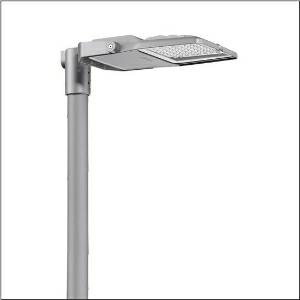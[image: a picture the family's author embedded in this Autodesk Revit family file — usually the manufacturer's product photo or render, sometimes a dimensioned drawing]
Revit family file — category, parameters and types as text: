
# Revit family: floodlight_fl_21_iq_mini___pl33t_5xa7771c2f3a_7d89
name_source: partatom
category: Lighting Fixtures
units: mm (PartAtom-declared; Revit-internal decimal feet)

## family parameters
Cut with Voids When Loaded = No
Host = Face
Light Source = No
Part Type = Normal
Room Calculation Point = No
Round Connector Dimension = Use Diameter
Shared = No

## types (1)
- --- (1 x LED, 12060 lm, 87.2 W, 3000K)
    Apparent Load = 87 VA
    CIE Flux Codes = 26 75 99 100 100
    Color Rendering = 70
    Color Temperature = 3000K
    Default Elevation = 1800 mm
    Description = Floodlight FL 21 iQ mini, floodlight, primary light control with lens, of PMMA, primary optical cover: protective disc, of toughened safety glass, transparent, light distribution: PL33T, light emission: direct distribution, installation type: surface-mounted, lamps: LED, High Power LED, rated values: 12.060lm | 87,2W | 138,3lm/W (begin service life); end service life: 12.060lm | 92,1W; at 50% lumin. flux: 6.030lm | 40,1W | 150,4lm/W, colour temperature: 3000K, colour rendering: CRI > 70, light colour: 730, light setting 1 begin service life: 100% | 12.060lm | 87,2W | 138,3lm/W | 3.000K, light setting 1 end service life: 92,1W, further light settings possible, control: Auto-Match, Temp-Guard, Lumen-Switch, Night-Set, Smart-Wire, Light-Fading, Desk-Remote (wireless, voltage-free reading and setting of iQ features in the workshop via application-optimized NFC function/RFID function), optimised constant luminous flux control (CLO 2.0), pre-setting: linear dimming characteristic, with terminal, 6-pole, mains connection: 220..240V, AC, 50/60Hz, luminaire housing, of diecast aluminium, powder-coated, SITECO metallic grey (DB 702S), corrosivity category C5 mid according to DIN EN ISO 12944suitable for swimming poolschlorine-resistant, sealing non-destructively replaceable, please order mast flange separately, mast bracket, of steel, galvanised, powder-coated, SITECO metallic grey (DB 702S), protection rating (complete): IP66, insulation class (complete): insulation class II (safety insulation), certification: CE, ENEC, VDE, protection symbol: D, impact resistance: IK08, permissible operating ambient temperature: -40..+40°C, permissible operating ambient temperature for outdoor applications: -40..+50°C, standard: DIN EN 12944, LABS conformity tested according to VDMA 24364:2018-05, packaging unit: 1 piece

Light Distribution: PL33T
    Height = 70 mm
    Lamp = 1 x LED
    Lamp Light Flux = 12060 lm
    Lamp Power = 87.2 W
    Lamp count = 1
    Length = 485 mm
    Luminous efficacy = 138 lm/W
    Manufacturer = Siteco
    ModVariant = No
    Model = 5XA7771C2F3A
    Number of Poles = 1
    OnlyDefault = Yes
    Power Factor = 1
    Product Name = Floodlight FL 21 iQ mini | PL33T
    Product group = floodlight | pylon annexe
    ProductGroupID = 6201
    Protection Class = Protection class II
    Protection Degree = IP 66
    RLX_Detail_Level = 1
    RLX_Emergency_Light_Flux = 0 lm
    RLX_Emergency_Type = 0
    RLX_Emergency_Type_DB = No
    RlxData = <blob elided: 101433 chars, md5=797fc2be>
    Socket = socket
    Standby Power = 0 W
    System Light Flux = 12060 lm
    System Power = 87 W
    Type Comments = factory setting: luminous flux: 100 % | dim-lin: 254 | 456 mA
    Type Image = l_1007125.jpg
    URL = http://relux.com
    VarID = @adj_149239
    Voltage = 0 V
    Weight = 0.00 kg
    Width = 337 mm

## geometry (parser evidence)
native form markers: Blend x4, Sweep x12
no freeform markers — native parametric forms only
